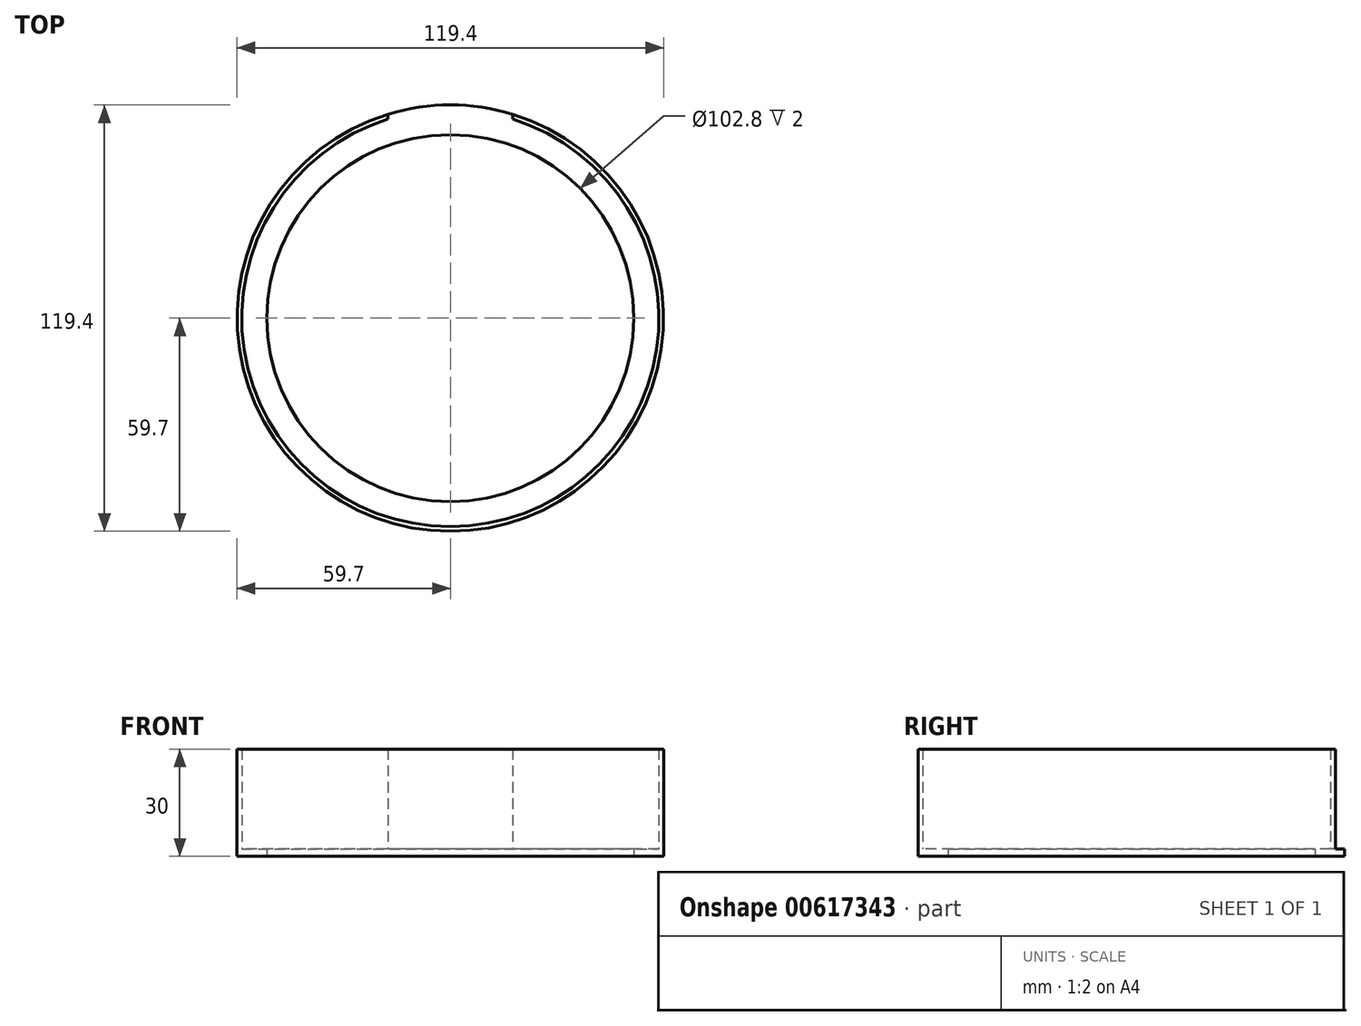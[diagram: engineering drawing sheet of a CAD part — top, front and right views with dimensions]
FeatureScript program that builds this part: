
annotation { "Feature Type Name" : "Feature", "Feature Type Description" : "" }
export const myFeature = defineFeature(function(context is Context, id is Id, definition is map)
    precondition{}
    {
        {
            var Q0;
            Q0=qCreatedBy(makeId("Top.planeOp"),FACE);
            var sketch = newSketch(context, id + "F0", { "sketchPlane" : qUnion([Q0])});
            skCircle(sketch, "E0", {"center": v(0, 0) * mm, "radius": 59.7 * mm});
            skCircle(sketch, "E1", {"center": v(0, 0) * mm, "radius": 51.4 * mm});
            skSolve(sketch);
        }
        {
            var Q0;
            Q0=makeQuery(id+"F0.imprint","IMPRINT",FACE,{"disambiguationData":[TD([[makeQuery(id+"F0.imprint","IMPRINT",EDGE,{"derivedFrom":sQuery(id+"F0.wireOp",EDGE,"E0")}),1.0]])]});
            extrude(context, id + "F1", {"entities" : qUnion([Q0]), "depth" : 2 * mm, "offsetDistance" : 25 * mm});
        }
        {
            var Q0;
            Q0=makeQuery(id+"F1.opExtrude","CAP_FACE",FACE,{"disambiguationData":[OSD([sQuery(id+"F0.wireOp",EDGE,"E0"),sQuery(id+"F0.wireOp",EDGE,"E1")])],"isStart":false});
            var sketch = newSketch(context, id + "F2", { "sketchPlane" : qUnion([Q0])});
            skArc(sketch, "E2", {"start": v(-17.4, 57.1) * mm, "mid": v(0, -59.7) * mm, "end": v(17.4, 57.1) * mm});
            skArc(sketch, "E3", {"start": v(-17.4, 55.75) * mm, "mid": v(0, -58.4) * mm, "end": v(17.4, 55.75) * mm});
            skLineSegment(sketch, "E4", {"start": v(-17.4, 57.1) * mm, "end": v(-17.4, 55.75) * mm});
            skLineSegment(sketch, "E5", {"start": v(17.4, 57.1) * mm, "end": v(17.4, 55.75) * mm});
            skSolve(sketch);
        }
        {
            var Q0;
            Q0=makeQuery(id+"F2.imprint","IMPRINT",FACE,{"disambiguationData":[TD([[makeQuery(id+"F2.imprint","IMPRINT",EDGE,{"derivedFrom":sQuery(id+"F2.wireOp",EDGE,"E2")}),1.0]])]});
            extrude(context, id + "F3", {"entities" : qUnion([Q0]), "operationType" : NewBodyOperationType.ADD, "depth" : 28 * mm, "offsetDistance" : 25 * mm});
        }
    });
